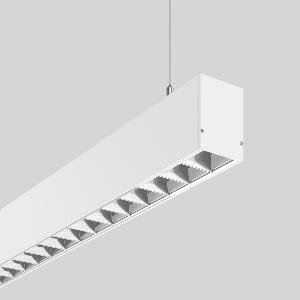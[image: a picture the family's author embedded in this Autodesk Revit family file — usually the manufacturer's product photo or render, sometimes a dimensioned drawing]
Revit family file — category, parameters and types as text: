
# Revit family: less_is_more_50_312338_002_1_76_19e7
name_source: partatom
category: Lighting Fixtures
units: mm (PartAtom-declared; Revit-internal decimal feet)

## family parameters
Cut with Voids When Loaded = No
Host = Face
Light Source = No
Part Type = Normal
Room Calculation Point = No
Round Connector Dimension = Use Diameter
Shared = No

## types (1)
- LESS IS MORE 50 (1 x LED Modul 840, 5300 lm, 4000)
    Apparent Load = 41 VA
    CIE Flux Codes = 95 100 100 100 100
    Color Rendering = 80
    Color Temperature = 4000
    Default Elevation = 1800 mm
    Description = Series: LESS IS MORE 50
Linear pendant luminaire for aesthetically sophisticated lighting. Housing: extruded aluminium profile, powder-coated. End cap aluminium powder-coated. Canopy made of aluminium, powder-coated. Alea optical system: Reflector structure (ABS, Aluminium-coated, highly polished) with integrated diffuser made of non-yellowing plastic (PMMA) opal for glare-free light at the workstation (screen-compliant according to EN 12464-1). Direct light emission. Suitable for pendant. 2-point steel cable suspension freely positionable and infinitely height-adjustable. Special lengths available on request. LED unit with integrated converter interchangeable and removable. Suitable for through-wiring. With sensors or as a safety luminaire on request. 
Colour: traffic white, matt (RAL 9016)
Length: 1687 mm
Width: 57 mm
Height: 75 mm
Suspension length: 2000 mm
Lamp: LED
Socket: without socket
Colour temperature: 4000K
Colour rendering index (CRI): 80
System power: 41 W
Rated luminous flux: 5300 lm
Luminous efficiency: 129 lm/W
Control gear: Converter, dimmable, DALI
Protection class: I
Type of protection: IP 20
    Height = 75 mm
    Lamp = 1 x LED Modul 840
    Lamp Light Flux = 5300 lm
    Lamp count = 1
    Length = 1687 mm
    Lifetime = 50000 h
    Luminous efficacy = 129 lm/W
    Manufacturer = RZB
    ModVariant = No
    Model = 312338.002.1.76
    Mounting Place = Ceiling
    Mounting Type = Pendant
    Number of Poles = 1
    OnlyDefault = Yes
    Power Factor = 1
    Product Name = LESS IS MORE 50
    Product group = Pendant LED linear luminaires
    ProductGroupID = 907
    Protection Class = Protection class I
    Protection Degree = IP 20
    RLX_Detail_Level = 1
    RLX_Emergency_Light_Flux = 0 lm
    RLX_Emergency_Type = 0
    RLX_Emergency_Type_DB = No
    RlxData = <blob elided: 33229 chars, md5=c9095f90>
    Socket = socket
    Standby Power = 0 W
    System Light Flux = 5300 lm
    System Power = 41 W
    Type Comments = Product without accessories
    Type Image = 312342.002.jpg
    URL = http://relux.com
    VarID = ---
    Voltage = 230 V
    Voltage Range = 220-240 V
    Weight = 0.00 kg
    Width = 57 mm

## geometry (parser evidence)
native form markers: Blend x4, Sweep x12
no freeform markers — native parametric forms only
